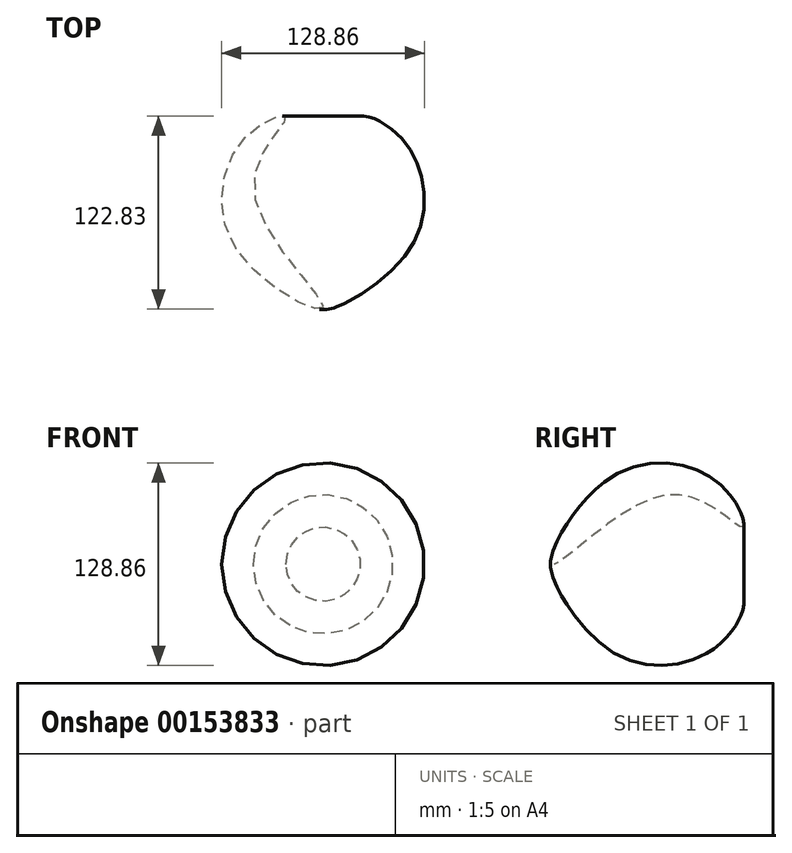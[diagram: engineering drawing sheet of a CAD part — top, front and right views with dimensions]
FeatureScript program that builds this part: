
annotation { "Feature Type Name" : "Feature", "Feature Type Description" : "" }
export const myFeature = defineFeature(function(context is Context, id is Id, definition is map)
    precondition{}
    {
        {
            var Q0;
            Q0=qCreatedBy(makeId("Top.planeOp"),FACE);
            var sketch = newSketch(context, id + "F1", { "sketchPlane" : qUnion([Q0])});
            skFitSpline(sketch, "E0", {"points": [v(-23.61, 45.27) * mm, v(-44.23, 0) * mm, v(0, -75.54) * mm, v(-54.73, -38.99) * mm, v(-48.14, 33.91) * mm, v(-23.61, 45.27) * mm]});
            skLineSegment(sketch, "E1", {"start": v(0, -75.54) * mm, "end": v(0, 21.77) * mm});
            skLineSegment(sketch, "E2", {"start": v(0, 21.77) * mm, "end": v(0, -26.89) * mm, "construction": true});
            skLineSegment(sketch, "E3", {"start": v(0, -26.89) * mm, "end": v(0, -26.89) * mm});
            skSolve(sketch);
        }
        {
            var Q0;
            {var subQ0=sQuery(id+"F1.wireOp",EDGE,"E1");var subQ1=sQuery(id+"F1.wireOp",EDGE,"E0");var subQ2=makeQuery(id+"F1.imprint","INTERSECT",VERTEX,{"disambiguationData":[OD(0.0)],"derivedFrom":[subQ1,subQ0]});Q0=makeQuery(id+"F1.imprint","IMPRINT",FACE,{"disambiguationData":[TD([[makeQuery(id+"F1.imprint","IMPRINT",EDGE,{"disambiguationData":[TD([[subQ2,-1.0]])],"derivedFrom":subQ1}),-1.0]])]});}
            var Q1;
            Q1=sQuery(id+"F1.wireOp",EDGE,"E1");
            revolve(context, id + "F0", {"entities" : qUnion([Q0]), "axis" : qUnion([Q1]), "revolveType" : RevolveType.FULL});
        }
    });
